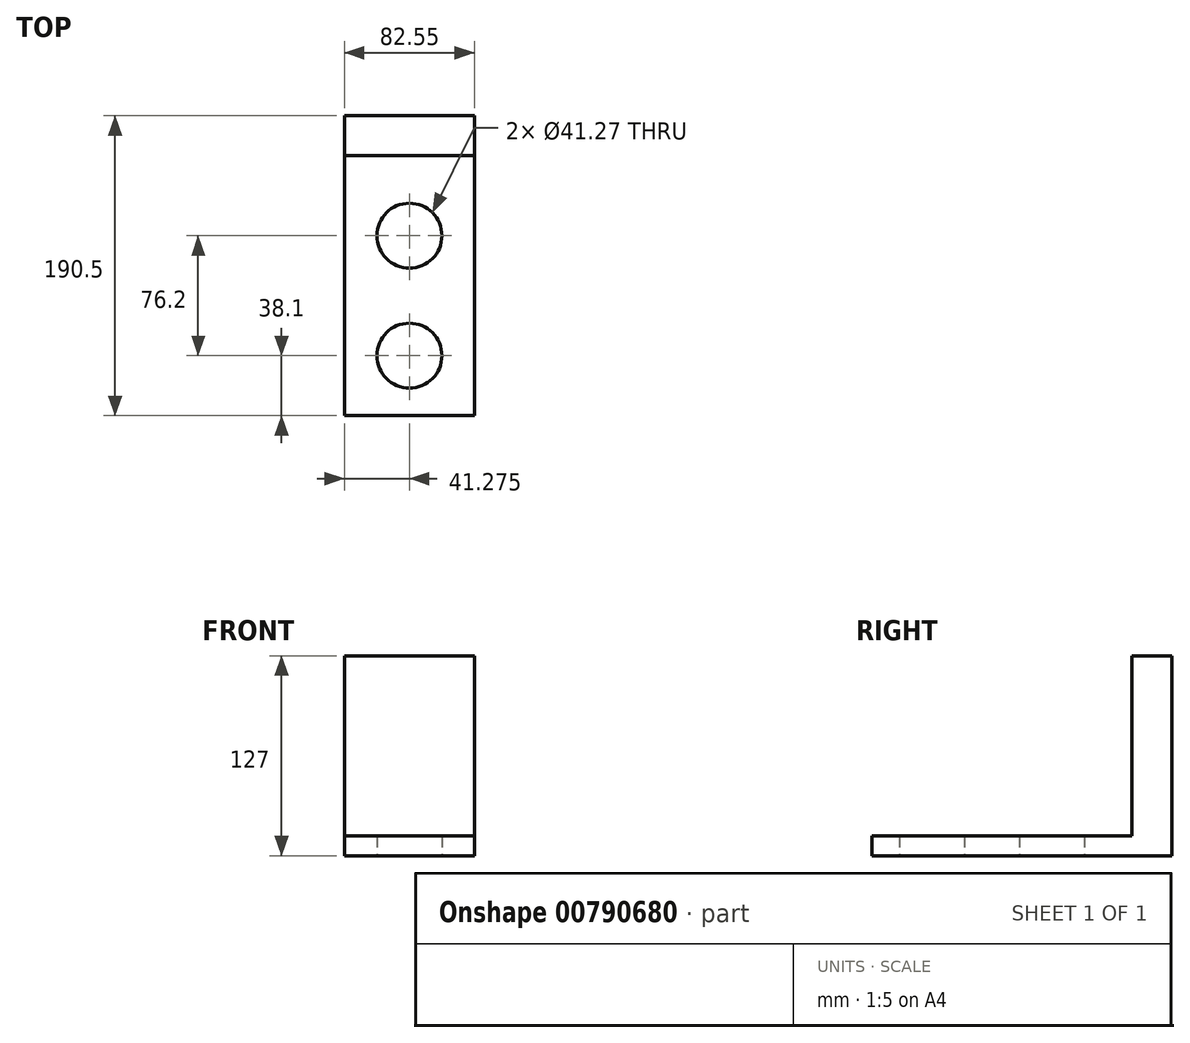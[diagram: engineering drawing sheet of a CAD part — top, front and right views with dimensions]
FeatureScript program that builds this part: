
annotation { "Feature Type Name" : "Feature", "Feature Type Description" : "" }
export const myFeature = defineFeature(function(context is Context, id is Id, definition is map)
    precondition{}
    {
        {
            var Q0;
            Q0=qCreatedBy(makeId("Front.planeOp"),FACE);
            var sketch = newSketch(context, id + "F0", { "sketchPlane" : qUnion([Q0])});
            skLineSegment(sketch, "E0", {"start": v(0, 0) * mm, "end": v(82.55, 0) * mm});
            skLineSegment(sketch, "E1", {"start": v(0, 0) * mm, "end": v(0, 12.7) * mm});
            skLineSegment(sketch, "E2", {"start": v(0, 12.7) * mm, "end": v(82.55, 12.7) * mm});
            skLineSegment(sketch, "E3", {"start": v(82.55, 12.7) * mm, "end": v(82.55, 0) * mm});
            skSolve(sketch);
        }
        {
            var Q0;
            Q0=makeQuery(id+"F0.imprint","IMPRINT",FACE,{"disambiguationData":[TD([[makeQuery(id+"F0.imprint","IMPRINT",EDGE,{"derivedFrom":sQuery(id+"F0.wireOp",EDGE,"E0")}),1.0]])]});
            extrude(context, id + "F1", {"entities" : qUnion([Q0]), "depth" : 190.5 * mm, "offsetDistance" : 25.4 * mm});
        }
        {
            var Q0;
            Q0=makeQuery(id+"F1.opExtrude","SWEPT_FACE",FACE,{"disambiguationData":[OSD([sQuery(id+"F0.wireOp",EDGE,"E0")])]});
            var sketch = newSketch(context, id + "F2", { "sketchPlane" : qUnion([Q0])});
            skLineSegment(sketch, "E4", {"start": v(41.28, 190.5) * mm, "end": v(41.28, 152.4) * mm, "construction": true});
            skLineSegment(sketch, "E5", {"start": v(41.28, 152.4) * mm, "end": v(41.28, 76.2) * mm, "construction": true});
            skCircle(sketch, "E6", {"center": v(41.28, 76.2) * mm, "radius": 20.64 * mm});
            skCircle(sketch, "E7", {"center": v(41.28, 152.4) * mm, "radius": 20.64 * mm});
            skSolve(sketch);
        }
        {
            var Q0;
            Q0=makeQuery(id+"F2.imprint","IMPRINT",FACE,{"disambiguationData":[TD([[makeQuery(id+"F2.imprint","IMPRINT",EDGE,{"derivedFrom":sQuery(id+"F2.wireOp",EDGE,"E6")}),1.0]])]});
            var sketch = newSketch(context, id + "F3", { "sketchPlane" : qUnion([Q0])});
            skSolve(sketch);
        }
        {
            var Q0;
            Q0=makeQuery(id+"F3.imprint","IMPRINT",FACE,{"disambiguationData":[TD([[makeQuery(id+"F3.imprint","IMPRINT",EDGE,{"derivedFrom":makeQuery(id+"F2.imprint","IMPRINT",EDGE,{"derivedFrom":sQuery(id+"F2.wireOp",EDGE,"E6")})}),1.0]])]});
            var Q1;
            Q1=makeQuery(id+"F2.imprint","IMPRINT",FACE,{"disambiguationData":[TD([[makeQuery(id+"F2.imprint","IMPRINT",EDGE,{"derivedFrom":sQuery(id+"F2.wireOp",EDGE,"E7")}),1.0]])]});
            extrude(context, id + "F4", {"entities" : qUnion([Q0, Q1]), "operationType" : NewBodyOperationType.REMOVE, "oppositeDirection" : true, "depth" : 25.4 * mm, "offsetDistance" : 25.4 * mm});
        }
        {
            var Q0;
            Q0=makeQuery(id+"F1.opExtrude","SWEPT_FACE",FACE,{"disambiguationData":[OSD([sQuery(id+"F0.wireOp",EDGE,"E2")])]});
            var sketch = newSketch(context, id + "F5", { "sketchPlane" : qUnion([Q0])});
            skLineSegment(sketch, "E8", {"start": v(0, 0) * mm, "end": v(0, -25.4) * mm});
            skLineSegment(sketch, "E9", {"start": v(0, -25.4) * mm, "end": v(82.55, -25.4) * mm});
            skLineSegment(sketch, "E10", {"start": v(82.55, -25.4) * mm, "end": v(82.55, 0) * mm});
            skLineSegment(sketch, "E11", {"start": v(82.55, 0) * mm, "end": v(0, 0) * mm});
            skSolve(sketch);
        }
        {
            var Q0;
            Q0=makeQuery(id+"F5.imprint","IMPRINT",FACE,{"disambiguationData":[TD([[makeQuery(id+"F5.imprint","IMPRINT",EDGE,{"derivedFrom":sQuery(id+"F5.wireOp",EDGE,"E8")}),-1.0]])]});
            var sketch = newSketch(context, id + "F6", { "sketchPlane" : qUnion([Q0])});
            skSolve(sketch);
        }
        {
            var Q0;
            Q0 = qSketchRegion(id + "F6", true);
            var Q1;
            Q1=makeQuery(id+"F5.imprint","IMPRINT",FACE,{"disambiguationData":[TD([[makeQuery(id+"F5.imprint","IMPRINT",EDGE,{"derivedFrom":sQuery(id+"F5.wireOp",EDGE,"E8")}),-1.0]])]});
            extrude(context, id + "F7", {"entities" : qUnion([Q0, Q1]), "operationType" : NewBodyOperationType.ADD, "depth" : 114.3 * mm, "offsetDistance" : 25.4 * mm});
        }
    });
